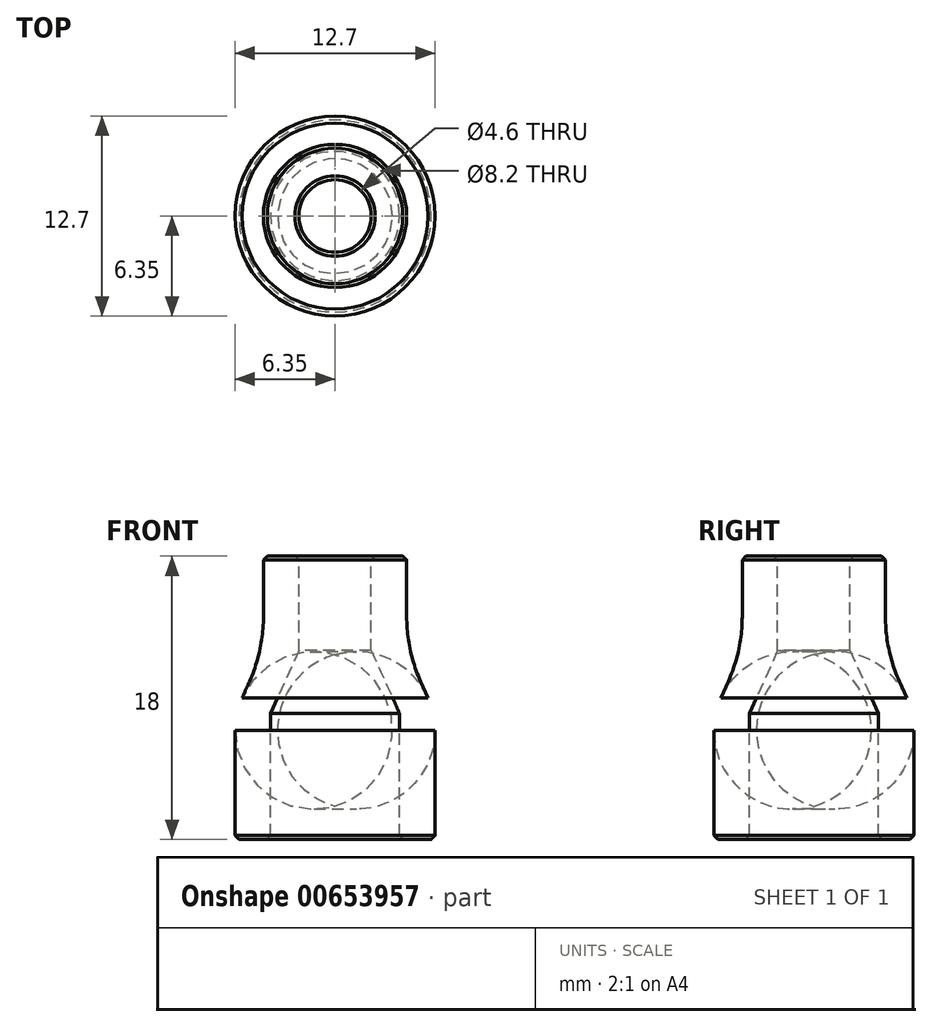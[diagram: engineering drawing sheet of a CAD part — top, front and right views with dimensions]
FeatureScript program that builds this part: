
annotation { "Feature Type Name" : "Feature", "Feature Type Description" : "" }
export const myFeature = defineFeature(function(context is Context, id is Id, definition is map)
    precondition{}
    {
        {
            var Q0;
            Q0=qCreatedBy(makeId("Front.planeOp"),FACE);
            var sketch = newSketch(context, id + "F0", { "sketchPlane" : qUnion([Q0])});
            skLineSegment(sketch, "E0", {"start": v(0, 0) * mm, "end": v(-4.1, 0) * mm, "construction": true});
            skLineSegment(sketch, "E1.bottom", {"start": v(-4.1, 0) * mm, "end": v(-6.35, 0) * mm});
            skLineSegment(sketch, "E1.top", {"start": v(-4.1, 8) * mm, "end": v(-6.35, 8) * mm});
            skLineSegment(sketch, "E1.left", {"start": v(-4.1, 0) * mm, "end": v(-4.1, 8) * mm});
            skLineSegment(sketch, "E1.right", {"start": v(-6.35, 0) * mm, "end": v(-6.35, 8) * mm});
            skLineSegment(sketch, "E2", {"start": v(0, 12) * mm, "end": v(-2.3, 12) * mm, "construction": true});
            skLineSegment(sketch, "E3", {"start": v(-4.1, 8) * mm, "end": v(-2.3, 12) * mm});
            skLineSegment(sketch, "E4", {"start": v(-6.35, 8) * mm, "end": v(-4.55, 12) * mm});
            skLineSegment(sketch, "E5.bottom", {"start": v(-2.3, 12) * mm, "end": v(-4.55, 12) * mm});
            skLineSegment(sketch, "E5.top", {"start": v(-2.3, 18) * mm, "end": v(-4.55, 18) * mm});
            skLineSegment(sketch, "E5.left", {"start": v(-2.3, 12) * mm, "end": v(-2.3, 18) * mm});
            skLineSegment(sketch, "E5.right", {"start": v(-4.55, 12) * mm, "end": v(-4.55, 18) * mm});
            skLineSegment(sketch, "E6", {"start": v(0, 22.7) * mm, "end": v(0, 0) * mm});
            skSolve(sketch);
        }
        {
            var Q0;
            Q0=makeQuery(id+"F0.imprint","IMPRINT",FACE,{"disambiguationData":[TD([[makeQuery(id+"F0.imprint","IMPRINT",EDGE,{"derivedFrom":sQuery(id+"F0.wireOp",EDGE,"E5.bottom")}),-1.0]])]});
            var Q1;
            Q1=makeQuery(id+"F0.imprint","IMPRINT",FACE,{"disambiguationData":[TD([[makeQuery(id+"F0.imprint","IMPRINT",EDGE,{"derivedFrom":sQuery(id+"F0.wireOp",EDGE,"E1.top")}),-1.0]])]});
            var Q2;
            Q2=makeQuery(id+"F0.imprint","IMPRINT",FACE,{"disambiguationData":[TD([[makeQuery(id+"F0.imprint","IMPRINT",EDGE,{"derivedFrom":sQuery(id+"F0.wireOp",EDGE,"E1.bottom")}),-1.0]])]});
            var Q3;
            Q3=sQuery(id+"F0.wireOp",EDGE,"E6");
            revolve(context, id + "F1", {"entities" : qUnion([Q0, Q1, Q2]), "axis" : qUnion([Q3]), "revolveType" : RevolveType.FULL});
        }
        {
            var Q0;
            Q0=makeQuery(id+"F1.opRevolve","SWEPT_FACE",FACE,{"disambiguationData":[OSD([sQuery(id+"F0.wireOp",EDGE,"E1.bottom")])]});
            chamfer(context, id + "F2", {"entities" : qUnion([Q0]), "width" : .25 * mm, "tangentPropagation" : true});
        }
        {
            var Q0;
            Q0=makeQuery(id+"F1.opRevolve","SWEPT_FACE",FACE,{"disambiguationData":[OSD([sQuery(id+"F0.wireOp",EDGE,"E5.top")])]});
            chamfer(context, id + "F3", {"entities" : qUnion([Q0]), "width" : .25 * mm, "tangentPropagation" : true});
        }
        {
            var Q0;
            Q0=makeQuery(id+"F1.opRevolve","SWEPT_EDGE",EDGE,{"disambiguationData":[OSD([sQuery(id+"F0.wireOp",EDGE,"E4"),sQuery(id+"F0.wireOp",EDGE,"E5.bottom"),sQuery(id+"F0.wireOp",EDGE,"E5.right")])]});
            fillet(context, id + "F4", {"entities" : qUnion([Q0]), "radius" : 10 * mm, "tangentPropagation" : true, "allowEdgeOverflow" : false});
        }
        {
            var Q0;
            Q0=makeQuery(id+"F1.opRevolve","SWEPT_EDGE",EDGE,{"disambiguationData":[OSD([sQuery(id+"F0.wireOp",EDGE,"E1.top"),sQuery(id+"F0.wireOp",EDGE,"E1.right"),sQuery(id+"F0.wireOp",EDGE,"E4")])]});
            fillet(context, id + "F5", {"entities" : qUnion([Q0]), "radius" : 5 * mm, "tangentPropagation" : true, "allowEdgeOverflow" : false});
        }
    });
